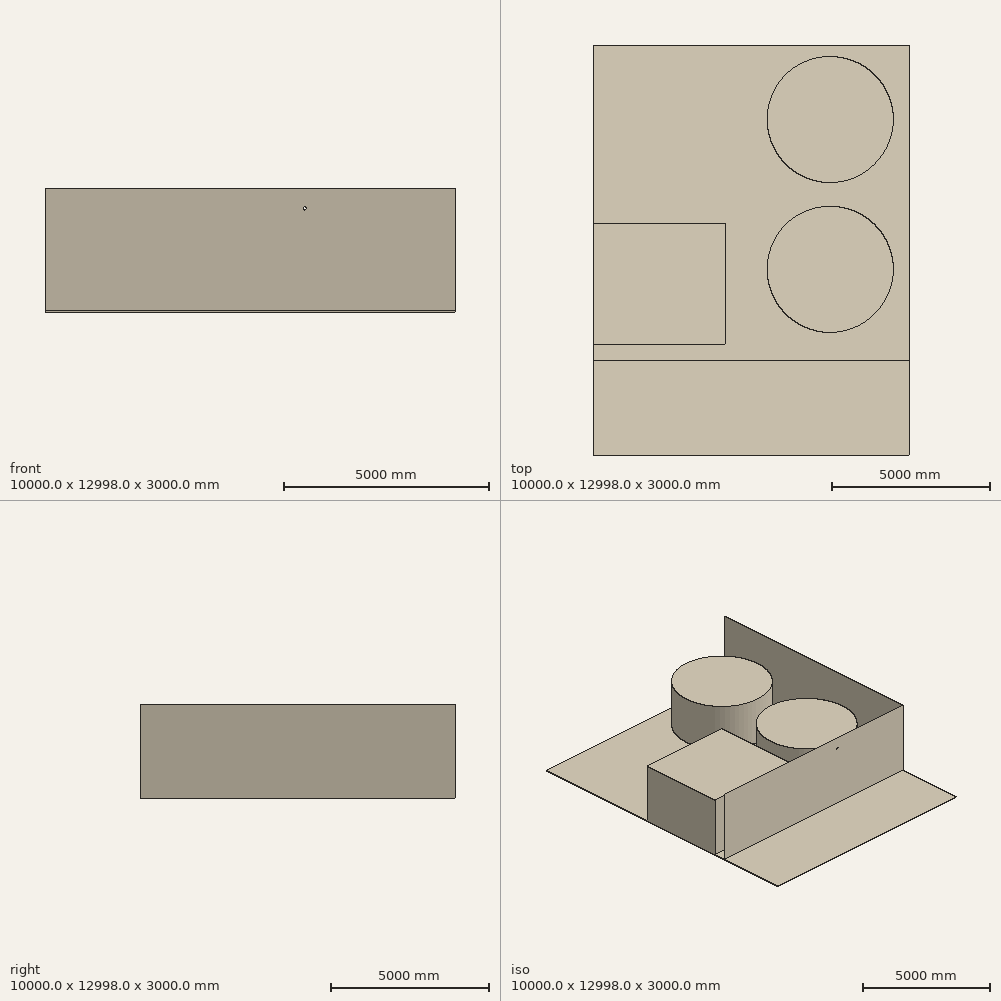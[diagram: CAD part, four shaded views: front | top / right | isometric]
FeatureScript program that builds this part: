
annotation { "Feature Type Name" : "Feature", "Feature Type Description" : "" }
export const myFeature = defineFeature(function(context is Context, id is Id, definition is map)
    precondition{}
    {
        {
            var Q0;
            Q0=qCreatedBy(makeId("Top.planeOp"),FACE);
            var sketch = newSketch(context, id + "F0", { "sketchPlane" : qUnion([Q0])});
            skLineSegment(sketch, "E0.bottom", {"start": v(-5000, 5000) * mm, "end": v(5000, 5000) * mm});
            skLineSegment(sketch, "E0.top", {"start": v(-5000, -5000) * mm, "end": v(5000, -5000) * mm});
            skLineSegment(sketch, "E0.left", {"start": v(-5000, 5000) * mm, "end": v(-5000, -5000) * mm});
            skLineSegment(sketch, "E0.right", {"start": v(5000, 5000) * mm, "end": v(5000, -5000) * mm});
            skPoint(sketch, "E0.middle", {"position": v(0, 0) * mm});
            skLineSegment(sketch, "E1", {"start": v(-5000, -4998) * mm, "end": v(4998, -4998) * mm});
            skLineSegment(sketch, "E2", {"start": v(4998, 5000) * mm, "end": v(4998, -4998) * mm});
            skCircle(sketch, "E3", {"center": v(2498, 2652) * mm, "radius": 2000 * mm});
            skCircle(sketch, "E4", {"center": v(2498, -2098) * mm, "radius": 2000 * mm});
            skLineSegment(sketch, "E5.top", {"start": v(-5000, -7998) * mm, "end": v(5000, -7998) * mm});
            skLineSegment(sketch, "E5.left", {"start": v(-5000, -4998) * mm, "end": v(-5000, -7998) * mm});
            skLineSegment(sketch, "E5.right", {"start": v(5000, -4998) * mm, "end": v(5000, -7998) * mm});
            skLineSegment(sketch, "E6.right", {"start": v(-5000, -3993.69) * mm, "end": v(-5000, -640.4) * mm});
            skSolve(sketch);
        }
        {
            var Q0;
            {var subQ2=sQuery(id+"F0.wireOp",EDGE,"E0.top");Q0=makeQuery(id+"F0.imprint","IMPRINT",FACE,{"disambiguationData":[TD([[makeQuery(id+"F0.imprint","IMPRINT",EDGE,{"derivedFrom":subQ2}),1.0]])]});}
            extrude(context, id + "F1", {"entities" : qUnion([Q0]), "depth" : 3000 * mm, "offsetDistance" : 25 * mm});
        }
        {
            var Q0;
            {var subQ4=sQuery(id+"F0.wireOp",EDGE,"E1");Q0=makeQuery(id+"F0.imprint","IMPRINT",FACE,{"disambiguationData":[TD([[makeQuery(id+"F0.imprint","IMPRINT",EDGE,{"derivedFrom":subQ4}),1.0]])]});}
            var Q1;
            Q1=makeQuery(id+"F0.imprint","IMPRINT",FACE,{"disambiguationData":[TD([[makeQuery(id+"F0.imprint","IMPRINT",EDGE,{"derivedFrom":sQuery(id+"F0.wireOp",EDGE,"E3")}),1.0]])]});
            var Q2;
            Q2=makeQuery(id+"F0.imprint","IMPRINT",FACE,{"disambiguationData":[TD([[makeQuery(id+"F0.imprint","IMPRINT",EDGE,{"derivedFrom":sQuery(id+"F0.wireOp",EDGE,"E4")}),1.0]])]});
            var Q3;
            {var subQ1=sQuery(id+"F0.wireOp",EDGE,"E0.left");Q3=makeQuery(id+"F0.imprint","IMPRINT",FACE,{"disambiguationData":[TD([[makeQuery(id+"F0.imprint","IMPRINT",EDGE,{"derivedFrom":subQ1}),1.0]])]});}
            var Q4;
            {var subQ5=sQuery(id+"F0.wireOp",EDGE,"E5.top");Q4=makeQuery(id+"F0.imprint","IMPRINT",FACE,{"disambiguationData":[TD([[makeQuery(id+"F0.imprint","IMPRINT",EDGE,{"derivedFrom":subQ5}),1.0]])]});}
            extrude(context, id + "F2", {"entities" : qUnion([Q0, Q1, Q2, Q3, Q4]), "operationType" : NewBodyOperationType.ADD, "depth" : 25 * mm, "offsetDistance" : 25 * mm});
        }
        {
            var Q0;
            Q0=makeQuery(id+"F0.imprint","IMPRINT",FACE,{"disambiguationData":[TD([[makeQuery(id+"F0.imprint","IMPRINT",EDGE,{"derivedFrom":sQuery(id+"F0.wireOp",EDGE,"E3")}),1.0]])]});
            var Q1;
            Q1=makeQuery(id+"F0.imprint","IMPRINT",FACE,{"disambiguationData":[TD([[makeQuery(id+"F0.imprint","IMPRINT",EDGE,{"derivedFrom":sQuery(id+"F0.wireOp",EDGE,"E4")}),1.0]])]});
            extrude(context, id + "F3", {"entities" : qUnion([Q0, Q1]), "depth" : 2000 * mm, "offsetDistance" : 25 * mm});
        }
        {
            var Q0;
            Q0=makeQuery(id+"F1.opExtrude","SWEPT_FACE",FACE,{"disambiguationData":[OSD([sQuery(id+"F0.wireOp",EDGE,"E0.top")])]});
            var sketch = newSketch(context, id + "F4", { "sketchPlane" : qUnion([Q0])});
            skLineSegment(sketch, "E7", {"start": v(5000, 25) * mm, "end": v(1330, 25) * mm, "construction": true});
            skLineSegment(sketch, "E8", {"start": v(1330, 25) * mm, "end": v(1330, 175) * mm, "construction": true});
            skPoint(sketch, "E9", {"position": v(1330, 175) * mm});
            skPoint(sketch, "E10", {"position": v(1330, 25) * mm});
            skLineSegment(sketch, "E11", {"start": v(1330, 175) * mm, "end": v(1330, 2525) * mm, "construction": true});
            skPoint(sketch, "E12", {"position": v(1330, 2525) * mm});
            skSolve(sketch);
        }
        {
            var Q0;
            Q0=sQuery(id+"F4.wireOp",VERTEX,"E12");
            var Q1;
            Q1=makeQuery(id+"F1.opExtrude","SWEPT_BODY",BODY,{"disambiguationData":[OSD([sQuery(id+"F0.wireOp",EDGE,"E0.bottom"),sQuery(id+"F0.wireOp",EDGE,"E0.top"),sQuery(id+"F0.wireOp",EDGE,"E0.right"),sQuery(id+"F0.wireOp",EDGE,"E2"),sQuery(id+"F0.wireOp",EDGE,"E1"),sQuery(id+"F0.wireOp",EDGE,"E5.left"),sQuery(id+"F0.wireOp",EDGE,"E5.right")])]});
            hole(context, id + "F5", {"style" : HoleStyle.SIMPLE, "endStyle" : HoleEndStyle.BLIND, "holeDiameter" : 75 * mm, "majorDiameter" : 5 * mm, "holeDepth" : 100 * mm, "isTappedThrough" : true, "tappedDepth" : 12 * mm, "tapClearance" : 3, "startFromSketch" : true, "locations" : qUnion([Q0]), "scope" : qUnion([Q1])});
        }
        {
            var Q0;
            Q0=makeQuery(id+"F2.opExtrude","CAP_FACE",FACE,{"disambiguationData":[OSD([sQuery(id+"F0.wireOp",EDGE,"E0.bottom"),sQuery(id+"F0.wireOp",EDGE,"E0.left"),sQuery(id+"F0.wireOp",EDGE,"E2"),sQuery(id+"F0.wireOp",EDGE,"E1"),sQuery(id+"F0.wireOp",EDGE,"E6.right")])],"isStart":false});
            var sketch = newSketch(context, id + "F6", { "sketchPlane" : qUnion([Q0])});
            skLineSegment(sketch, "E13.bottom", {"start": v(-819.04, -4467.8) * mm, "end": v(-5000, -4467.8) * mm});
            skLineSegment(sketch, "E13.top", {"start": v(-819.04, -641.26) * mm, "end": v(-5000, -641.26) * mm});
            skLineSegment(sketch, "E13.left", {"start": v(-819.04, -4467.8) * mm, "end": v(-819.04, -641.26) * mm});
            skLineSegment(sketch, "E13.right", {"start": v(-5000, -4467.8) * mm, "end": v(-5000, -641.26) * mm});
            skSolve(sketch);
        }
        {
            var Q0;
            Q0 = qSketchRegion(id + "F6", true);
            extrude(context, id + "F7", {"entities" : qUnion([Q0]), "operationType" : NewBodyOperationType.ADD, "depth" : 2500 * mm, "offsetDistance" : 25 * mm});
        }
    });
